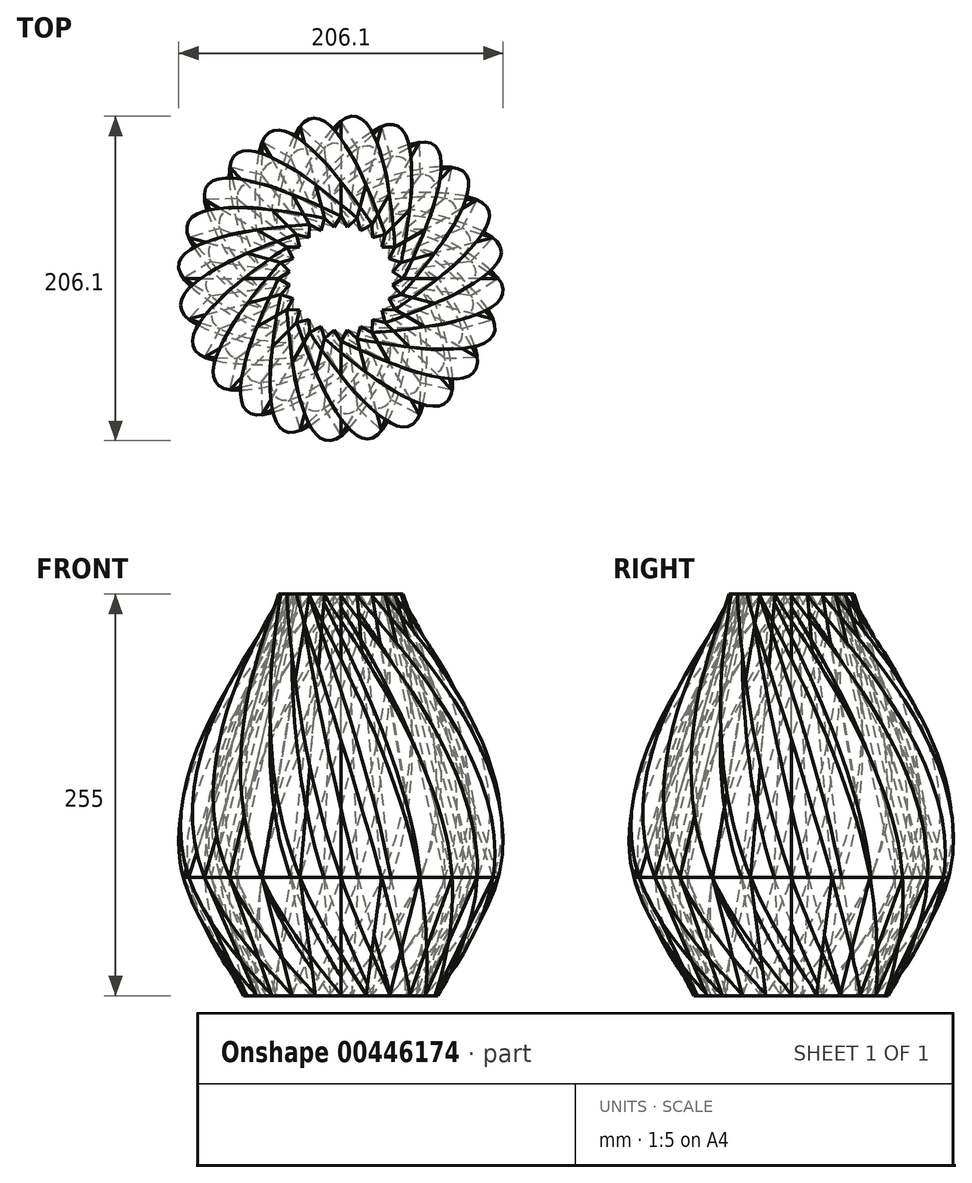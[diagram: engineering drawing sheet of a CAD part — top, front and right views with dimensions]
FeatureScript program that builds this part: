
annotation { "Feature Type Name" : "Feature", "Feature Type Description" : "" }
export const myFeature = defineFeature(function(context is Context, id is Id, definition is map)
    precondition{}
    {
        {
            var Q0;
            Q0=qCreatedBy(makeId("Top.planeOp"),FACE);
            var sketch = newSketch(context, id + "F0", { "sketchPlane" : qUnion([Q0])});
            skCircle(sketch, "E0", {"center": v(0, 0) * mm, "radius": 100 * mm, "construction": true});
            skLineSegment(sketch, "E1", {"start": v(-10.85, 82.43) * mm, "end": v(0, 100) * mm});
            skLineSegment(sketch, "E2.MirrorCS", {"start": v(10.85, 82.43) * mm, "end": v(0, 100) * mm});
            skLineSegment(sketch, "E3.1.0", {"start": v(-31.82, 76.82) * mm, "end": v(-25.88, 96.6) * mm});
            skLineSegment(sketch, "E3.1.1", {"start": v(-10.85, 82.43) * mm, "end": v(-25.88, 96.6) * mm});
            skLineSegment(sketch, "E3.2.0", {"start": v(-50.62, 65.96) * mm, "end": v(-50, 86.6) * mm});
            skLineSegment(sketch, "E3.2.1", {"start": v(-31.82, 76.82) * mm, "end": v(-50, 86.6) * mm});
            skLineSegment(sketch, "E3.3.0", {"start": v(-65.96, 50.62) * mm, "end": v(-70.71, 70.71) * mm});
            skLineSegment(sketch, "E3.3.1", {"start": v(-50.62, 65.96) * mm, "end": v(-70.71, 70.71) * mm});
            skLineSegment(sketch, "E3.4.0", {"start": v(-76.82, 31.82) * mm, "end": v(-86.6, 50) * mm});
            skLineSegment(sketch, "E3.4.1", {"start": v(-65.96, 50.62) * mm, "end": v(-86.6, 50) * mm});
            skLineSegment(sketch, "E3.5.0", {"start": v(-82.43, 10.85) * mm, "end": v(-96.6, 25.88) * mm});
            skLineSegment(sketch, "E3.5.1", {"start": v(-76.82, 31.82) * mm, "end": v(-96.6, 25.88) * mm});
            skLineSegment(sketch, "E3.6.0", {"start": v(-82.43, -10.85) * mm, "end": v(-100, 0) * mm});
            skLineSegment(sketch, "E3.6.1", {"start": v(-82.43, 10.85) * mm, "end": v(-100, 0) * mm});
            skLineSegment(sketch, "E3.7.0", {"start": v(-76.82, -31.82) * mm, "end": v(-96.6, -25.88) * mm});
            skLineSegment(sketch, "E3.7.1", {"start": v(-82.43, -10.85) * mm, "end": v(-96.6, -25.88) * mm});
            skLineSegment(sketch, "E3.8.0", {"start": v(-65.96, -50.62) * mm, "end": v(-86.6, -50) * mm});
            skLineSegment(sketch, "E3.8.1", {"start": v(-76.82, -31.82) * mm, "end": v(-86.6, -50) * mm});
            skLineSegment(sketch, "E3.9.0", {"start": v(-50.62, -65.96) * mm, "end": v(-70.71, -70.71) * mm});
            skLineSegment(sketch, "E3.9.1", {"start": v(-65.96, -50.62) * mm, "end": v(-70.71, -70.71) * mm});
            skLineSegment(sketch, "E3.10.0", {"start": v(-31.82, -76.82) * mm, "end": v(-50, -86.6) * mm});
            skLineSegment(sketch, "E3.10.1", {"start": v(-50.62, -65.96) * mm, "end": v(-50, -86.6) * mm});
            skLineSegment(sketch, "E3.11.0", {"start": v(-10.85, -82.43) * mm, "end": v(-25.88, -96.6) * mm});
            skLineSegment(sketch, "E3.11.1", {"start": v(-31.82, -76.82) * mm, "end": v(-25.88, -96.6) * mm});
            skLineSegment(sketch, "E3.12.0", {"start": v(10.85, -82.43) * mm, "end": v(0, -100) * mm});
            skLineSegment(sketch, "E3.12.1", {"start": v(-10.85, -82.43) * mm, "end": v(0, -100) * mm});
            skLineSegment(sketch, "E3.13.0", {"start": v(31.82, -76.82) * mm, "end": v(25.88, -96.6) * mm});
            skLineSegment(sketch, "E3.13.1", {"start": v(10.85, -82.43) * mm, "end": v(25.88, -96.6) * mm});
            skLineSegment(sketch, "E3.14.0", {"start": v(50.62, -65.96) * mm, "end": v(50, -86.6) * mm});
            skLineSegment(sketch, "E3.14.1", {"start": v(31.82, -76.82) * mm, "end": v(50, -86.6) * mm});
            skLineSegment(sketch, "E3.15.0", {"start": v(65.96, -50.62) * mm, "end": v(70.71, -70.71) * mm});
            skLineSegment(sketch, "E3.15.1", {"start": v(50.62, -65.96) * mm, "end": v(70.71, -70.71) * mm});
            skLineSegment(sketch, "E3.16.0", {"start": v(76.82, -31.82) * mm, "end": v(86.6, -50) * mm});
            skLineSegment(sketch, "E3.16.1", {"start": v(65.96, -50.62) * mm, "end": v(86.6, -50) * mm});
            skLineSegment(sketch, "E3.17.0", {"start": v(82.43, -10.85) * mm, "end": v(96.6, -25.88) * mm});
            skLineSegment(sketch, "E3.17.1", {"start": v(76.82, -31.82) * mm, "end": v(96.6, -25.88) * mm});
            skLineSegment(sketch, "E3.18.0", {"start": v(82.43, 10.85) * mm, "end": v(100, 0) * mm});
            skLineSegment(sketch, "E3.18.1", {"start": v(82.43, -10.85) * mm, "end": v(100, 0) * mm});
            skLineSegment(sketch, "E3.19.0", {"start": v(76.82, 31.82) * mm, "end": v(96.6, 25.88) * mm});
            skLineSegment(sketch, "E3.19.1", {"start": v(82.43, 10.85) * mm, "end": v(96.6, 25.88) * mm});
            skLineSegment(sketch, "E3.20.0", {"start": v(65.96, 50.62) * mm, "end": v(86.6, 50) * mm});
            skLineSegment(sketch, "E3.20.1", {"start": v(76.82, 31.82) * mm, "end": v(86.6, 50) * mm});
            skLineSegment(sketch, "E3.21.0", {"start": v(50.62, 65.96) * mm, "end": v(70.71, 70.71) * mm});
            skLineSegment(sketch, "E3.21.1", {"start": v(65.96, 50.62) * mm, "end": v(70.71, 70.71) * mm});
            skLineSegment(sketch, "E3.22.0", {"start": v(31.82, 76.82) * mm, "end": v(50, 86.6) * mm});
            skLineSegment(sketch, "E3.22.1", {"start": v(50.62, 65.96) * mm, "end": v(50, 86.6) * mm});
            skLineSegment(sketch, "E3.23.0", {"start": v(10.85, 82.43) * mm, "end": v(25.88, 96.6) * mm});
            skLineSegment(sketch, "E3.23.1", {"start": v(31.82, 76.82) * mm, "end": v(25.88, 96.6) * mm});
            skSolve(sketch);
        }
        {
            var Q0;
            Q0=makeQuery(id+"F0.imprint","IMPRINT",FACE,{"disambiguationData":[TD([[makeQuery(id+"F0.imprint","IMPRINT",EDGE,{"derivedFrom":sQuery(id+"F0.wireOp",EDGE,"E1")}),-1.0]])]});
            extrude(context, id + "F1", {"entities" : qUnion([Q0]), "depth" : 180 * mm, "hasDraft" : true, "draftAngle" : 10 * degree, "draftPullDirection" : true});
        }
        {
            var Q1;
            Q1=makeQuery(id+"F1.opExtrude","CAP_FACE",FACE,{"disambiguationData":[OSD([sQuery(id+"F0.wireOp",EDGE,"E1"),sQuery(id+"F0.wireOp",EDGE,"E2.MirrorCS"),sQuery(id+"F0.wireOp",EDGE,"E3.1.0"),sQuery(id+"F0.wireOp",EDGE,"E3.1.1"),sQuery(id+"F0.wireOp",EDGE,"E3.2.0"),sQuery(id+"F0.wireOp",EDGE,"E3.2.1"),sQuery(id+"F0.wireOp",EDGE,"E3.3.0"),sQuery(id+"F0.wireOp",EDGE,"E3.3.1"),sQuery(id+"F0.wireOp",EDGE,"E3.4.0"),sQuery(id+"F0.wireOp",EDGE,"E3.4.1"),sQuery(id+"F0.wireOp",EDGE,"E3.5.0"),sQuery(id+"F0.wireOp",EDGE,"E3.5.1"),sQuery(id+"F0.wireOp",EDGE,"E3.6.0"),sQuery(id+"F0.wireOp",EDGE,"E3.6.1"),sQuery(id+"F0.wireOp",EDGE,"E3.7.0"),sQuery(id+"F0.wireOp",EDGE,"E3.7.1"),sQuery(id+"F0.wireOp",EDGE,"E3.8.0"),sQuery(id+"F0.wireOp",EDGE,"E3.8.1"),sQuery(id+"F0.wireOp",EDGE,"E3.9.0"),sQuery(id+"F0.wireOp",EDGE,"E3.9.1"),sQuery(id+"F0.wireOp",EDGE,"E3.10.0"),sQuery(id+"F0.wireOp",EDGE,"E3.10.1"),sQuery(id+"F0.wireOp",EDGE,"E3.11.0"),sQuery(id+"F0.wireOp",EDGE,"E3.11.1"),sQuery(id+"F0.wireOp",EDGE,"E3.12.0"),sQuery(id+"F0.wireOp",EDGE,"E3.12.1"),sQuery(id+"F0.wireOp",EDGE,"E3.13.0"),sQuery(id+"F0.wireOp",EDGE,"E3.13.1"),sQuery(id+"F0.wireOp",EDGE,"E3.14.0"),sQuery(id+"F0.wireOp",EDGE,"E3.14.1"),sQuery(id+"F0.wireOp",EDGE,"E3.15.0"),sQuery(id+"F0.wireOp",EDGE,"E3.15.1"),sQuery(id+"F0.wireOp",EDGE,"E3.16.0"),sQuery(id+"F0.wireOp",EDGE,"E3.16.1"),sQuery(id+"F0.wireOp",EDGE,"E3.17.0"),sQuery(id+"F0.wireOp",EDGE,"E3.17.1"),sQuery(id+"F0.wireOp",EDGE,"E3.18.0"),sQuery(id+"F0.wireOp",EDGE,"E3.18.1"),sQuery(id+"F0.wireOp",EDGE,"E3.19.0"),sQuery(id+"F0.wireOp",EDGE,"E3.19.1"),sQuery(id+"F0.wireOp",EDGE,"E3.20.0"),sQuery(id+"F0.wireOp",EDGE,"E3.20.1"),sQuery(id+"F0.wireOp",EDGE,"E3.21.0"),sQuery(id+"F0.wireOp",EDGE,"E3.21.1"),sQuery(id+"F0.wireOp",EDGE,"E3.22.0"),sQuery(id+"F0.wireOp",EDGE,"E3.22.1"),sQuery(id+"F0.wireOp",EDGE,"E3.23.0"),sQuery(id+"F0.wireOp",EDGE,"E3.23.1"),sQuery(id+"F0.wireOp",EDGE,"E3.24.0"),sQuery(id+"F0.wireOp",EDGE,"E3.24.1"),sQuery(id+"F0.wireOp",EDGE,"E3.25.0"),sQuery(id+"F0.wireOp",EDGE,"E3.25.1"),sQuery(id+"F0.wireOp",EDGE,"E3.26.0"),sQuery(id+"F0.wireOp",EDGE,"E3.26.1"),sQuery(id+"F0.wireOp",EDGE,"E3.27.0"),sQuery(id+"F0.wireOp",EDGE,"E3.27.1"),sQuery(id+"F0.wireOp",EDGE,"E3.28.0"),sQuery(id+"F0.wireOp",EDGE,"E3.28.1"),sQuery(id+"F0.wireOp",EDGE,"E3.29.0"),sQuery(id+"F0.wireOp",EDGE,"E3.29.1"),sQuery(id+"F0.wireOp",EDGE,"E3.30.0"),sQuery(id+"F0.wireOp",EDGE,"E3.30.1"),sQuery(id+"F0.wireOp",EDGE,"E3.31.0"),sQuery(id+"F0.wireOp",EDGE,"E3.31.1"),sQuery(id+"F0.wireOp",EDGE,"E3.32.0"),sQuery(id+"F0.wireOp",EDGE,"E3.32.1"),sQuery(id+"F0.wireOp",EDGE,"E3.33.0"),sQuery(id+"F0.wireOp",EDGE,"E3.33.1"),sQuery(id+"F0.wireOp",EDGE,"E3.34.0"),sQuery(id+"F0.wireOp",EDGE,"E3.34.1"),sQuery(id+"F0.wireOp",EDGE,"E3.35.0"),sQuery(id+"F0.wireOp",EDGE,"E3.35.1")])],"isStart":false});
            var Q2;
            Q2=makeQuery(id+"F1.opExtrude","CAP_FACE",FACE,{"disambiguationData":[OSD([sQuery(id+"F0.wireOp",EDGE,"E1"),sQuery(id+"F0.wireOp",EDGE,"E2.MirrorCS"),sQuery(id+"F0.wireOp",EDGE,"E3.1.0"),sQuery(id+"F0.wireOp",EDGE,"E3.1.1"),sQuery(id+"F0.wireOp",EDGE,"E3.2.0"),sQuery(id+"F0.wireOp",EDGE,"E3.2.1"),sQuery(id+"F0.wireOp",EDGE,"E3.3.0"),sQuery(id+"F0.wireOp",EDGE,"E3.3.1"),sQuery(id+"F0.wireOp",EDGE,"E3.4.0"),sQuery(id+"F0.wireOp",EDGE,"E3.4.1"),sQuery(id+"F0.wireOp",EDGE,"E3.5.0"),sQuery(id+"F0.wireOp",EDGE,"E3.5.1"),sQuery(id+"F0.wireOp",EDGE,"E3.6.0"),sQuery(id+"F0.wireOp",EDGE,"E3.6.1"),sQuery(id+"F0.wireOp",EDGE,"E3.7.0"),sQuery(id+"F0.wireOp",EDGE,"E3.7.1"),sQuery(id+"F0.wireOp",EDGE,"E3.8.0"),sQuery(id+"F0.wireOp",EDGE,"E3.8.1"),sQuery(id+"F0.wireOp",EDGE,"E3.9.0"),sQuery(id+"F0.wireOp",EDGE,"E3.9.1"),sQuery(id+"F0.wireOp",EDGE,"E3.10.0"),sQuery(id+"F0.wireOp",EDGE,"E3.10.1"),sQuery(id+"F0.wireOp",EDGE,"E3.11.0"),sQuery(id+"F0.wireOp",EDGE,"E3.11.1"),sQuery(id+"F0.wireOp",EDGE,"E3.12.0"),sQuery(id+"F0.wireOp",EDGE,"E3.12.1"),sQuery(id+"F0.wireOp",EDGE,"E3.13.0"),sQuery(id+"F0.wireOp",EDGE,"E3.13.1"),sQuery(id+"F0.wireOp",EDGE,"E3.14.0"),sQuery(id+"F0.wireOp",EDGE,"E3.14.1"),sQuery(id+"F0.wireOp",EDGE,"E3.15.0"),sQuery(id+"F0.wireOp",EDGE,"E3.15.1"),sQuery(id+"F0.wireOp",EDGE,"E3.16.0"),sQuery(id+"F0.wireOp",EDGE,"E3.16.1"),sQuery(id+"F0.wireOp",EDGE,"E3.17.0"),sQuery(id+"F0.wireOp",EDGE,"E3.17.1"),sQuery(id+"F0.wireOp",EDGE,"E3.18.0"),sQuery(id+"F0.wireOp",EDGE,"E3.18.1"),sQuery(id+"F0.wireOp",EDGE,"E3.19.0"),sQuery(id+"F0.wireOp",EDGE,"E3.19.1"),sQuery(id+"F0.wireOp",EDGE,"E3.20.0"),sQuery(id+"F0.wireOp",EDGE,"E3.20.1"),sQuery(id+"F0.wireOp",EDGE,"E3.21.0"),sQuery(id+"F0.wireOp",EDGE,"E3.21.1"),sQuery(id+"F0.wireOp",EDGE,"E3.22.0"),sQuery(id+"F0.wireOp",EDGE,"E3.22.1"),sQuery(id+"F0.wireOp",EDGE,"E3.23.0"),sQuery(id+"F0.wireOp",EDGE,"E3.23.1"),sQuery(id+"F0.wireOp",EDGE,"E3.24.0"),sQuery(id+"F0.wireOp",EDGE,"E3.24.1"),sQuery(id+"F0.wireOp",EDGE,"E3.25.0"),sQuery(id+"F0.wireOp",EDGE,"E3.25.1"),sQuery(id+"F0.wireOp",EDGE,"E3.26.0"),sQuery(id+"F0.wireOp",EDGE,"E3.26.1"),sQuery(id+"F0.wireOp",EDGE,"E3.27.0"),sQuery(id+"F0.wireOp",EDGE,"E3.27.1"),sQuery(id+"F0.wireOp",EDGE,"E3.28.0"),sQuery(id+"F0.wireOp",EDGE,"E3.28.1"),sQuery(id+"F0.wireOp",EDGE,"E3.29.0"),sQuery(id+"F0.wireOp",EDGE,"E3.29.1"),sQuery(id+"F0.wireOp",EDGE,"E3.30.0"),sQuery(id+"F0.wireOp",EDGE,"E3.30.1"),sQuery(id+"F0.wireOp",EDGE,"E3.31.0"),sQuery(id+"F0.wireOp",EDGE,"E3.31.1"),sQuery(id+"F0.wireOp",EDGE,"E3.32.0"),sQuery(id+"F0.wireOp",EDGE,"E3.32.1"),sQuery(id+"F0.wireOp",EDGE,"E3.33.0"),sQuery(id+"F0.wireOp",EDGE,"E3.33.1"),sQuery(id+"F0.wireOp",EDGE,"E3.34.0"),sQuery(id+"F0.wireOp",EDGE,"E3.34.1"),sQuery(id+"F0.wireOp",EDGE,"E3.35.0"),sQuery(id+"F0.wireOp",EDGE,"E3.35.1")])],"isStart":true});
            var Q3;
            Q3=makeQuery(id+"F1.opExtrude","CAP_VERTEX",VERTEX,{"disambiguationData":[OSD([sQuery(id+"F0.wireOp",EDGE,"E3.18.0"),sQuery(id+"F0.wireOp",EDGE,"E3.18.1")])],"isStart":true});
            var Q4;
            Q4=makeQuery(id+"F1.opExtrude","CAP_VERTEX",VERTEX,{"disambiguationData":[OSD([sQuery(id+"F0.wireOp",EDGE,"E3.22.0"),sQuery(id+"F0.wireOp",EDGE,"E3.22.1")])],"isStart":false});
            loft(context, id + "F2", {"endCondition" : LoftEndDerivativeType.NORMAL_TO_PROFILE, "endMagnitude" : 2, "sheetProfilesArray" : [{ "sheetProfileEntities" : qUnion([Q1]) }, { "sheetProfileEntities" : qUnion([Q2]) }], "matchConnections" : true, "connections" : [{ "connectionEntities" : qUnion([Q3, Q4]), "connectionEdgeQueries" : qUnion([]), "connectionEdgeParameters" : [] }]});
        }
        {
            var Q0;
            Q0=makeQuery(id+"F2.opLoft","SWEPT_BODY",BODY,{"disambiguationData":[OSD([sQuery(id+"F0.wireOp",EDGE,"E1"),sQuery(id+"F0.wireOp",EDGE,"E2.MirrorCS"),sQuery(id+"F0.wireOp",EDGE,"E3.1.0"),sQuery(id+"F0.wireOp",EDGE,"E3.1.1"),sQuery(id+"F0.wireOp",EDGE,"E3.2.0"),sQuery(id+"F0.wireOp",EDGE,"E3.2.1"),sQuery(id+"F0.wireOp",EDGE,"E3.3.0"),sQuery(id+"F0.wireOp",EDGE,"E3.3.1"),sQuery(id+"F0.wireOp",EDGE,"E3.4.0"),sQuery(id+"F0.wireOp",EDGE,"E3.4.1"),sQuery(id+"F0.wireOp",EDGE,"E3.5.0"),sQuery(id+"F0.wireOp",EDGE,"E3.5.1"),sQuery(id+"F0.wireOp",EDGE,"E3.6.0"),sQuery(id+"F0.wireOp",EDGE,"E3.6.1"),sQuery(id+"F0.wireOp",EDGE,"E3.7.0"),sQuery(id+"F0.wireOp",EDGE,"E3.7.1"),sQuery(id+"F0.wireOp",EDGE,"E3.8.0"),sQuery(id+"F0.wireOp",EDGE,"E3.8.1"),sQuery(id+"F0.wireOp",EDGE,"E3.9.0"),sQuery(id+"F0.wireOp",EDGE,"E3.9.1"),sQuery(id+"F0.wireOp",EDGE,"E3.10.0"),sQuery(id+"F0.wireOp",EDGE,"E3.10.1"),sQuery(id+"F0.wireOp",EDGE,"E3.11.0"),sQuery(id+"F0.wireOp",EDGE,"E3.11.1"),sQuery(id+"F0.wireOp",EDGE,"E3.12.0"),sQuery(id+"F0.wireOp",EDGE,"E3.12.1"),sQuery(id+"F0.wireOp",EDGE,"E3.13.0"),sQuery(id+"F0.wireOp",EDGE,"E3.13.1"),sQuery(id+"F0.wireOp",EDGE,"E3.14.0"),sQuery(id+"F0.wireOp",EDGE,"E3.14.1"),sQuery(id+"F0.wireOp",EDGE,"E3.15.0"),sQuery(id+"F0.wireOp",EDGE,"E3.15.1"),sQuery(id+"F0.wireOp",EDGE,"E3.16.0"),sQuery(id+"F0.wireOp",EDGE,"E3.16.1"),sQuery(id+"F0.wireOp",EDGE,"E3.17.0"),sQuery(id+"F0.wireOp",EDGE,"E3.17.1"),sQuery(id+"F0.wireOp",EDGE,"E3.18.0"),sQuery(id+"F0.wireOp",EDGE,"E3.18.1"),sQuery(id+"F0.wireOp",EDGE,"E3.19.0"),sQuery(id+"F0.wireOp",EDGE,"E3.19.1"),sQuery(id+"F0.wireOp",EDGE,"E3.20.0"),sQuery(id+"F0.wireOp",EDGE,"E3.20.1"),sQuery(id+"F0.wireOp",EDGE,"E3.21.0"),sQuery(id+"F0.wireOp",EDGE,"E3.21.1"),sQuery(id+"F0.wireOp",EDGE,"E3.22.0"),sQuery(id+"F0.wireOp",EDGE,"E3.22.1"),sQuery(id+"F0.wireOp",EDGE,"E3.23.0"),sQuery(id+"F0.wireOp",EDGE,"E3.23.1"),sQuery(id+"F0.wireOp",EDGE,"E3.24.0"),sQuery(id+"F0.wireOp",EDGE,"E3.24.1"),sQuery(id+"F0.wireOp",EDGE,"E3.25.0"),sQuery(id+"F0.wireOp",EDGE,"E3.25.1"),sQuery(id+"F0.wireOp",EDGE,"E3.26.0"),sQuery(id+"F0.wireOp",EDGE,"E3.26.1"),sQuery(id+"F0.wireOp",EDGE,"E3.27.0"),sQuery(id+"F0.wireOp",EDGE,"E3.27.1"),sQuery(id+"F0.wireOp",EDGE,"E3.28.0"),sQuery(id+"F0.wireOp",EDGE,"E3.28.1"),sQuery(id+"F0.wireOp",EDGE,"E3.29.0"),sQuery(id+"F0.wireOp",EDGE,"E3.29.1"),sQuery(id+"F0.wireOp",EDGE,"E3.30.0"),sQuery(id+"F0.wireOp",EDGE,"E3.30.1"),sQuery(id+"F0.wireOp",EDGE,"E3.31.0"),sQuery(id+"F0.wireOp",EDGE,"E3.31.1"),sQuery(id+"F0.wireOp",EDGE,"E3.32.0"),sQuery(id+"F0.wireOp",EDGE,"E3.32.1"),sQuery(id+"F0.wireOp",EDGE,"E3.33.0"),sQuery(id+"F0.wireOp",EDGE,"E3.33.1"),sQuery(id+"F0.wireOp",EDGE,"E3.34.0"),sQuery(id+"F0.wireOp",EDGE,"E3.34.1"),sQuery(id+"F0.wireOp",EDGE,"E3.35.0"),sQuery(id+"F0.wireOp",EDGE,"E3.35.1")])]});
            deleteBodies(context, id + "F3", {"entities" : qUnion([Q0])});
        }
        {
            var Q0;
            Q0=makeQuery(id+"F1.opExtrude","CAP_FACE",FACE,{"disambiguationData":[OSD([sQuery(id+"F0.wireOp",EDGE,"E1"),sQuery(id+"F0.wireOp",EDGE,"E2.MirrorCS"),sQuery(id+"F0.wireOp",EDGE,"E3.1.0"),sQuery(id+"F0.wireOp",EDGE,"E3.1.1"),sQuery(id+"F0.wireOp",EDGE,"E3.2.0"),sQuery(id+"F0.wireOp",EDGE,"E3.2.1"),sQuery(id+"F0.wireOp",EDGE,"E3.3.0"),sQuery(id+"F0.wireOp",EDGE,"E3.3.1"),sQuery(id+"F0.wireOp",EDGE,"E3.4.0"),sQuery(id+"F0.wireOp",EDGE,"E3.4.1"),sQuery(id+"F0.wireOp",EDGE,"E3.5.0"),sQuery(id+"F0.wireOp",EDGE,"E3.5.1"),sQuery(id+"F0.wireOp",EDGE,"E3.6.0"),sQuery(id+"F0.wireOp",EDGE,"E3.6.1"),sQuery(id+"F0.wireOp",EDGE,"E3.7.0"),sQuery(id+"F0.wireOp",EDGE,"E3.7.1"),sQuery(id+"F0.wireOp",EDGE,"E3.8.0"),sQuery(id+"F0.wireOp",EDGE,"E3.8.1"),sQuery(id+"F0.wireOp",EDGE,"E3.9.0"),sQuery(id+"F0.wireOp",EDGE,"E3.9.1"),sQuery(id+"F0.wireOp",EDGE,"E3.10.0"),sQuery(id+"F0.wireOp",EDGE,"E3.10.1"),sQuery(id+"F0.wireOp",EDGE,"E3.11.0"),sQuery(id+"F0.wireOp",EDGE,"E3.11.1"),sQuery(id+"F0.wireOp",EDGE,"E3.12.0"),sQuery(id+"F0.wireOp",EDGE,"E3.12.1"),sQuery(id+"F0.wireOp",EDGE,"E3.13.0"),sQuery(id+"F0.wireOp",EDGE,"E3.13.1"),sQuery(id+"F0.wireOp",EDGE,"E3.14.0"),sQuery(id+"F0.wireOp",EDGE,"E3.14.1"),sQuery(id+"F0.wireOp",EDGE,"E3.15.0"),sQuery(id+"F0.wireOp",EDGE,"E3.15.1"),sQuery(id+"F0.wireOp",EDGE,"E3.16.0"),sQuery(id+"F0.wireOp",EDGE,"E3.16.1"),sQuery(id+"F0.wireOp",EDGE,"E3.17.0"),sQuery(id+"F0.wireOp",EDGE,"E3.17.1"),sQuery(id+"F0.wireOp",EDGE,"E3.18.0"),sQuery(id+"F0.wireOp",EDGE,"E3.18.1"),sQuery(id+"F0.wireOp",EDGE,"E3.19.0"),sQuery(id+"F0.wireOp",EDGE,"E3.19.1"),sQuery(id+"F0.wireOp",EDGE,"E3.20.0"),sQuery(id+"F0.wireOp",EDGE,"E3.20.1"),sQuery(id+"F0.wireOp",EDGE,"E3.21.0"),sQuery(id+"F0.wireOp",EDGE,"E3.21.1"),sQuery(id+"F0.wireOp",EDGE,"E3.22.0"),sQuery(id+"F0.wireOp",EDGE,"E3.22.1"),sQuery(id+"F0.wireOp",EDGE,"E3.23.0"),sQuery(id+"F0.wireOp",EDGE,"E3.23.1"),sQuery(id+"F0.wireOp",EDGE,"E3.24.0"),sQuery(id+"F0.wireOp",EDGE,"E3.24.1"),sQuery(id+"F0.wireOp",EDGE,"E3.25.0"),sQuery(id+"F0.wireOp",EDGE,"E3.25.1"),sQuery(id+"F0.wireOp",EDGE,"E3.26.0"),sQuery(id+"F0.wireOp",EDGE,"E3.26.1"),sQuery(id+"F0.wireOp",EDGE,"E3.27.0"),sQuery(id+"F0.wireOp",EDGE,"E3.27.1"),sQuery(id+"F0.wireOp",EDGE,"E3.28.0"),sQuery(id+"F0.wireOp",EDGE,"E3.28.1"),sQuery(id+"F0.wireOp",EDGE,"E3.29.0"),sQuery(id+"F0.wireOp",EDGE,"E3.29.1"),sQuery(id+"F0.wireOp",EDGE,"E3.30.0"),sQuery(id+"F0.wireOp",EDGE,"E3.30.1"),sQuery(id+"F0.wireOp",EDGE,"E3.31.0"),sQuery(id+"F0.wireOp",EDGE,"E3.31.1"),sQuery(id+"F0.wireOp",EDGE,"E3.32.0"),sQuery(id+"F0.wireOp",EDGE,"E3.32.1"),sQuery(id+"F0.wireOp",EDGE,"E3.33.0"),sQuery(id+"F0.wireOp",EDGE,"E3.33.1"),sQuery(id+"F0.wireOp",EDGE,"E3.34.0"),sQuery(id+"F0.wireOp",EDGE,"E3.34.1"),sQuery(id+"F0.wireOp",EDGE,"E3.35.0"),sQuery(id+"F0.wireOp",EDGE,"E3.35.1")])],"isStart":true});
            extrude(context, id + "F4", {"entities" : qUnion([Q0]), "depth" : 75 * mm, "hasDraft" : true, "draftAngle" : 15 * degree, "draftPullDirection" : true});
        }
        {
            var Q1;
            Q1=makeQuery(id+"F1.opExtrude","CAP_FACE",FACE,{"disambiguationData":[OSD([sQuery(id+"F0.wireOp",EDGE,"E1"),sQuery(id+"F0.wireOp",EDGE,"E2.MirrorCS"),sQuery(id+"F0.wireOp",EDGE,"E3.1.0"),sQuery(id+"F0.wireOp",EDGE,"E3.1.1"),sQuery(id+"F0.wireOp",EDGE,"E3.2.0"),sQuery(id+"F0.wireOp",EDGE,"E3.2.1"),sQuery(id+"F0.wireOp",EDGE,"E3.3.0"),sQuery(id+"F0.wireOp",EDGE,"E3.3.1"),sQuery(id+"F0.wireOp",EDGE,"E3.4.0"),sQuery(id+"F0.wireOp",EDGE,"E3.4.1"),sQuery(id+"F0.wireOp",EDGE,"E3.5.0"),sQuery(id+"F0.wireOp",EDGE,"E3.5.1"),sQuery(id+"F0.wireOp",EDGE,"E3.6.0"),sQuery(id+"F0.wireOp",EDGE,"E3.6.1"),sQuery(id+"F0.wireOp",EDGE,"E3.7.0"),sQuery(id+"F0.wireOp",EDGE,"E3.7.1"),sQuery(id+"F0.wireOp",EDGE,"E3.8.0"),sQuery(id+"F0.wireOp",EDGE,"E3.8.1"),sQuery(id+"F0.wireOp",EDGE,"E3.9.0"),sQuery(id+"F0.wireOp",EDGE,"E3.9.1"),sQuery(id+"F0.wireOp",EDGE,"E3.10.0"),sQuery(id+"F0.wireOp",EDGE,"E3.10.1"),sQuery(id+"F0.wireOp",EDGE,"E3.11.0"),sQuery(id+"F0.wireOp",EDGE,"E3.11.1"),sQuery(id+"F0.wireOp",EDGE,"E3.12.0"),sQuery(id+"F0.wireOp",EDGE,"E3.12.1"),sQuery(id+"F0.wireOp",EDGE,"E3.13.0"),sQuery(id+"F0.wireOp",EDGE,"E3.13.1"),sQuery(id+"F0.wireOp",EDGE,"E3.14.0"),sQuery(id+"F0.wireOp",EDGE,"E3.14.1"),sQuery(id+"F0.wireOp",EDGE,"E3.15.0"),sQuery(id+"F0.wireOp",EDGE,"E3.15.1"),sQuery(id+"F0.wireOp",EDGE,"E3.16.0"),sQuery(id+"F0.wireOp",EDGE,"E3.16.1"),sQuery(id+"F0.wireOp",EDGE,"E3.17.0"),sQuery(id+"F0.wireOp",EDGE,"E3.17.1"),sQuery(id+"F0.wireOp",EDGE,"E3.18.0"),sQuery(id+"F0.wireOp",EDGE,"E3.18.1"),sQuery(id+"F0.wireOp",EDGE,"E3.19.0"),sQuery(id+"F0.wireOp",EDGE,"E3.19.1"),sQuery(id+"F0.wireOp",EDGE,"E3.20.0"),sQuery(id+"F0.wireOp",EDGE,"E3.20.1"),sQuery(id+"F0.wireOp",EDGE,"E3.21.0"),sQuery(id+"F0.wireOp",EDGE,"E3.21.1"),sQuery(id+"F0.wireOp",EDGE,"E3.22.0"),sQuery(id+"F0.wireOp",EDGE,"E3.22.1"),sQuery(id+"F0.wireOp",EDGE,"E3.23.0"),sQuery(id+"F0.wireOp",EDGE,"E3.23.1"),sQuery(id+"F0.wireOp",EDGE,"E3.24.0"),sQuery(id+"F0.wireOp",EDGE,"E3.24.1"),sQuery(id+"F0.wireOp",EDGE,"E3.25.0"),sQuery(id+"F0.wireOp",EDGE,"E3.25.1"),sQuery(id+"F0.wireOp",EDGE,"E3.26.0"),sQuery(id+"F0.wireOp",EDGE,"E3.26.1"),sQuery(id+"F0.wireOp",EDGE,"E3.27.0"),sQuery(id+"F0.wireOp",EDGE,"E3.27.1"),sQuery(id+"F0.wireOp",EDGE,"E3.28.0"),sQuery(id+"F0.wireOp",EDGE,"E3.28.1"),sQuery(id+"F0.wireOp",EDGE,"E3.29.0"),sQuery(id+"F0.wireOp",EDGE,"E3.29.1"),sQuery(id+"F0.wireOp",EDGE,"E3.30.0"),sQuery(id+"F0.wireOp",EDGE,"E3.30.1"),sQuery(id+"F0.wireOp",EDGE,"E3.31.0"),sQuery(id+"F0.wireOp",EDGE,"E3.31.1"),sQuery(id+"F0.wireOp",EDGE,"E3.32.0"),sQuery(id+"F0.wireOp",EDGE,"E3.32.1"),sQuery(id+"F0.wireOp",EDGE,"E3.33.0"),sQuery(id+"F0.wireOp",EDGE,"E3.33.1"),sQuery(id+"F0.wireOp",EDGE,"E3.34.0"),sQuery(id+"F0.wireOp",EDGE,"E3.34.1"),sQuery(id+"F0.wireOp",EDGE,"E3.35.0"),sQuery(id+"F0.wireOp",EDGE,"E3.35.1")])],"isStart":false});
            var Q2;
            Q2=makeQuery(id+"F1.opExtrude","CAP_FACE",FACE,{"disambiguationData":[OSD([sQuery(id+"F0.wireOp",EDGE,"E1"),sQuery(id+"F0.wireOp",EDGE,"E2.MirrorCS"),sQuery(id+"F0.wireOp",EDGE,"E3.1.0"),sQuery(id+"F0.wireOp",EDGE,"E3.1.1"),sQuery(id+"F0.wireOp",EDGE,"E3.2.0"),sQuery(id+"F0.wireOp",EDGE,"E3.2.1"),sQuery(id+"F0.wireOp",EDGE,"E3.3.0"),sQuery(id+"F0.wireOp",EDGE,"E3.3.1"),sQuery(id+"F0.wireOp",EDGE,"E3.4.0"),sQuery(id+"F0.wireOp",EDGE,"E3.4.1"),sQuery(id+"F0.wireOp",EDGE,"E3.5.0"),sQuery(id+"F0.wireOp",EDGE,"E3.5.1"),sQuery(id+"F0.wireOp",EDGE,"E3.6.0"),sQuery(id+"F0.wireOp",EDGE,"E3.6.1"),sQuery(id+"F0.wireOp",EDGE,"E3.7.0"),sQuery(id+"F0.wireOp",EDGE,"E3.7.1"),sQuery(id+"F0.wireOp",EDGE,"E3.8.0"),sQuery(id+"F0.wireOp",EDGE,"E3.8.1"),sQuery(id+"F0.wireOp",EDGE,"E3.9.0"),sQuery(id+"F0.wireOp",EDGE,"E3.9.1"),sQuery(id+"F0.wireOp",EDGE,"E3.10.0"),sQuery(id+"F0.wireOp",EDGE,"E3.10.1"),sQuery(id+"F0.wireOp",EDGE,"E3.11.0"),sQuery(id+"F0.wireOp",EDGE,"E3.11.1"),sQuery(id+"F0.wireOp",EDGE,"E3.12.0"),sQuery(id+"F0.wireOp",EDGE,"E3.12.1"),sQuery(id+"F0.wireOp",EDGE,"E3.13.0"),sQuery(id+"F0.wireOp",EDGE,"E3.13.1"),sQuery(id+"F0.wireOp",EDGE,"E3.14.0"),sQuery(id+"F0.wireOp",EDGE,"E3.14.1"),sQuery(id+"F0.wireOp",EDGE,"E3.15.0"),sQuery(id+"F0.wireOp",EDGE,"E3.15.1"),sQuery(id+"F0.wireOp",EDGE,"E3.16.0"),sQuery(id+"F0.wireOp",EDGE,"E3.16.1"),sQuery(id+"F0.wireOp",EDGE,"E3.17.0"),sQuery(id+"F0.wireOp",EDGE,"E3.17.1"),sQuery(id+"F0.wireOp",EDGE,"E3.18.0"),sQuery(id+"F0.wireOp",EDGE,"E3.18.1"),sQuery(id+"F0.wireOp",EDGE,"E3.19.0"),sQuery(id+"F0.wireOp",EDGE,"E3.19.1"),sQuery(id+"F0.wireOp",EDGE,"E3.20.0"),sQuery(id+"F0.wireOp",EDGE,"E3.20.1"),sQuery(id+"F0.wireOp",EDGE,"E3.21.0"),sQuery(id+"F0.wireOp",EDGE,"E3.21.1"),sQuery(id+"F0.wireOp",EDGE,"E3.22.0"),sQuery(id+"F0.wireOp",EDGE,"E3.22.1"),sQuery(id+"F0.wireOp",EDGE,"E3.23.0"),sQuery(id+"F0.wireOp",EDGE,"E3.23.1"),sQuery(id+"F0.wireOp",EDGE,"E3.24.0"),sQuery(id+"F0.wireOp",EDGE,"E3.24.1"),sQuery(id+"F0.wireOp",EDGE,"E3.25.0"),sQuery(id+"F0.wireOp",EDGE,"E3.25.1"),sQuery(id+"F0.wireOp",EDGE,"E3.26.0"),sQuery(id+"F0.wireOp",EDGE,"E3.26.1"),sQuery(id+"F0.wireOp",EDGE,"E3.27.0"),sQuery(id+"F0.wireOp",EDGE,"E3.27.1"),sQuery(id+"F0.wireOp",EDGE,"E3.28.0"),sQuery(id+"F0.wireOp",EDGE,"E3.28.1"),sQuery(id+"F0.wireOp",EDGE,"E3.29.0"),sQuery(id+"F0.wireOp",EDGE,"E3.29.1"),sQuery(id+"F0.wireOp",EDGE,"E3.30.0"),sQuery(id+"F0.wireOp",EDGE,"E3.30.1"),sQuery(id+"F0.wireOp",EDGE,"E3.31.0"),sQuery(id+"F0.wireOp",EDGE,"E3.31.1"),sQuery(id+"F0.wireOp",EDGE,"E3.32.0"),sQuery(id+"F0.wireOp",EDGE,"E3.32.1"),sQuery(id+"F0.wireOp",EDGE,"E3.33.0"),sQuery(id+"F0.wireOp",EDGE,"E3.33.1"),sQuery(id+"F0.wireOp",EDGE,"E3.34.0"),sQuery(id+"F0.wireOp",EDGE,"E3.34.1"),sQuery(id+"F0.wireOp",EDGE,"E3.35.0"),sQuery(id+"F0.wireOp",EDGE,"E3.35.1")])],"isStart":true});
            var Q3;
            Q3=makeQuery(id+"F4.opExtrude","CAP_FACE",FACE,{"disambiguationData":[OSD([sQuery(id+"F0.wireOp",EDGE,"E1"),sQuery(id+"F0.wireOp",EDGE,"E2.MirrorCS"),sQuery(id+"F0.wireOp",EDGE,"E3.1.0"),sQuery(id+"F0.wireOp",EDGE,"E3.1.1"),sQuery(id+"F0.wireOp",EDGE,"E3.2.0"),sQuery(id+"F0.wireOp",EDGE,"E3.2.1"),sQuery(id+"F0.wireOp",EDGE,"E3.3.0"),sQuery(id+"F0.wireOp",EDGE,"E3.3.1"),sQuery(id+"F0.wireOp",EDGE,"E3.4.0"),sQuery(id+"F0.wireOp",EDGE,"E3.4.1"),sQuery(id+"F0.wireOp",EDGE,"E3.5.0"),sQuery(id+"F0.wireOp",EDGE,"E3.5.1"),sQuery(id+"F0.wireOp",EDGE,"E3.6.0"),sQuery(id+"F0.wireOp",EDGE,"E3.6.1"),sQuery(id+"F0.wireOp",EDGE,"E3.7.0"),sQuery(id+"F0.wireOp",EDGE,"E3.7.1"),sQuery(id+"F0.wireOp",EDGE,"E3.8.0"),sQuery(id+"F0.wireOp",EDGE,"E3.8.1"),sQuery(id+"F0.wireOp",EDGE,"E3.9.0"),sQuery(id+"F0.wireOp",EDGE,"E3.9.1"),sQuery(id+"F0.wireOp",EDGE,"E3.10.0"),sQuery(id+"F0.wireOp",EDGE,"E3.10.1"),sQuery(id+"F0.wireOp",EDGE,"E3.11.0"),sQuery(id+"F0.wireOp",EDGE,"E3.11.1"),sQuery(id+"F0.wireOp",EDGE,"E3.12.0"),sQuery(id+"F0.wireOp",EDGE,"E3.12.1"),sQuery(id+"F0.wireOp",EDGE,"E3.13.0"),sQuery(id+"F0.wireOp",EDGE,"E3.13.1"),sQuery(id+"F0.wireOp",EDGE,"E3.14.0"),sQuery(id+"F0.wireOp",EDGE,"E3.14.1"),sQuery(id+"F0.wireOp",EDGE,"E3.15.0"),sQuery(id+"F0.wireOp",EDGE,"E3.15.1"),sQuery(id+"F0.wireOp",EDGE,"E3.16.0"),sQuery(id+"F0.wireOp",EDGE,"E3.16.1"),sQuery(id+"F0.wireOp",EDGE,"E3.17.0"),sQuery(id+"F0.wireOp",EDGE,"E3.17.1"),sQuery(id+"F0.wireOp",EDGE,"E3.18.0"),sQuery(id+"F0.wireOp",EDGE,"E3.18.1"),sQuery(id+"F0.wireOp",EDGE,"E3.19.0"),sQuery(id+"F0.wireOp",EDGE,"E3.19.1"),sQuery(id+"F0.wireOp",EDGE,"E3.20.0"),sQuery(id+"F0.wireOp",EDGE,"E3.20.1"),sQuery(id+"F0.wireOp",EDGE,"E3.21.0"),sQuery(id+"F0.wireOp",EDGE,"E3.21.1"),sQuery(id+"F0.wireOp",EDGE,"E3.22.0"),sQuery(id+"F0.wireOp",EDGE,"E3.22.1"),sQuery(id+"F0.wireOp",EDGE,"E3.23.0"),sQuery(id+"F0.wireOp",EDGE,"E3.23.1"),sQuery(id+"F0.wireOp",EDGE,"E3.24.0"),sQuery(id+"F0.wireOp",EDGE,"E3.24.1"),sQuery(id+"F0.wireOp",EDGE,"E3.25.0"),sQuery(id+"F0.wireOp",EDGE,"E3.25.1"),sQuery(id+"F0.wireOp",EDGE,"E3.26.0"),sQuery(id+"F0.wireOp",EDGE,"E3.26.1"),sQuery(id+"F0.wireOp",EDGE,"E3.27.0"),sQuery(id+"F0.wireOp",EDGE,"E3.27.1"),sQuery(id+"F0.wireOp",EDGE,"E3.28.0"),sQuery(id+"F0.wireOp",EDGE,"E3.28.1"),sQuery(id+"F0.wireOp",EDGE,"E3.29.0"),sQuery(id+"F0.wireOp",EDGE,"E3.29.1"),sQuery(id+"F0.wireOp",EDGE,"E3.30.0"),sQuery(id+"F0.wireOp",EDGE,"E3.30.1"),sQuery(id+"F0.wireOp",EDGE,"E3.31.0"),sQuery(id+"F0.wireOp",EDGE,"E3.31.1"),sQuery(id+"F0.wireOp",EDGE,"E3.32.0"),sQuery(id+"F0.wireOp",EDGE,"E3.32.1"),sQuery(id+"F0.wireOp",EDGE,"E3.33.0"),sQuery(id+"F0.wireOp",EDGE,"E3.33.1"),sQuery(id+"F0.wireOp",EDGE,"E3.34.0"),sQuery(id+"F0.wireOp",EDGE,"E3.34.1"),sQuery(id+"F0.wireOp",EDGE,"E3.35.0"),sQuery(id+"F0.wireOp",EDGE,"E3.35.1")])],"isStart":false});
            var Q4;
            Q4=makeQuery(id+"F1.opExtrude","CAP_VERTEX",VERTEX,{"disambiguationData":[OSD([sQuery(id+"F0.wireOp",EDGE,"E3.12.0"),sQuery(id+"F0.wireOp",EDGE,"E3.12.1")])],"isStart":true});
            var Q5;
            Q5=makeQuery(id+"F4.opExtrude","CAP_VERTEX",VERTEX,{"disambiguationData":[OSD([sQuery(id+"F0.wireOp",EDGE,"E3.14.0"),sQuery(id+"F0.wireOp",EDGE,"E3.14.1")])],"isStart":false});
            var Q6;
            Q6=makeQuery(id+"F1.opExtrude","CAP_VERTEX",VERTEX,{"disambiguationData":[OSD([sQuery(id+"F0.wireOp",EDGE,"E3.8.0"),sQuery(id+"F0.wireOp",EDGE,"E3.8.1")])],"isStart":false});
            loft(context, id + "F5", {"startCondition" : LoftEndDerivativeType.NORMAL_TO_PROFILE, "startMagnitude" : .1, "endCondition" : LoftEndDerivativeType.MATCH_TANGENT, "endMagnitude" : .1, "sheetProfilesArray" : [{ "sheetProfileEntities" : qUnion([Q1]) }, { "sheetProfileEntities" : qUnion([Q2]) }, { "sheetProfileEntities" : qUnion([Q3]) }], "matchConnections" : true, "connections" : [{ "connectionEntities" : qUnion([Q4, Q5, Q6]), "connectionEdgeQueries" : qUnion([]), "connectionEdgeParameters" : [] }]});
        }
    });
